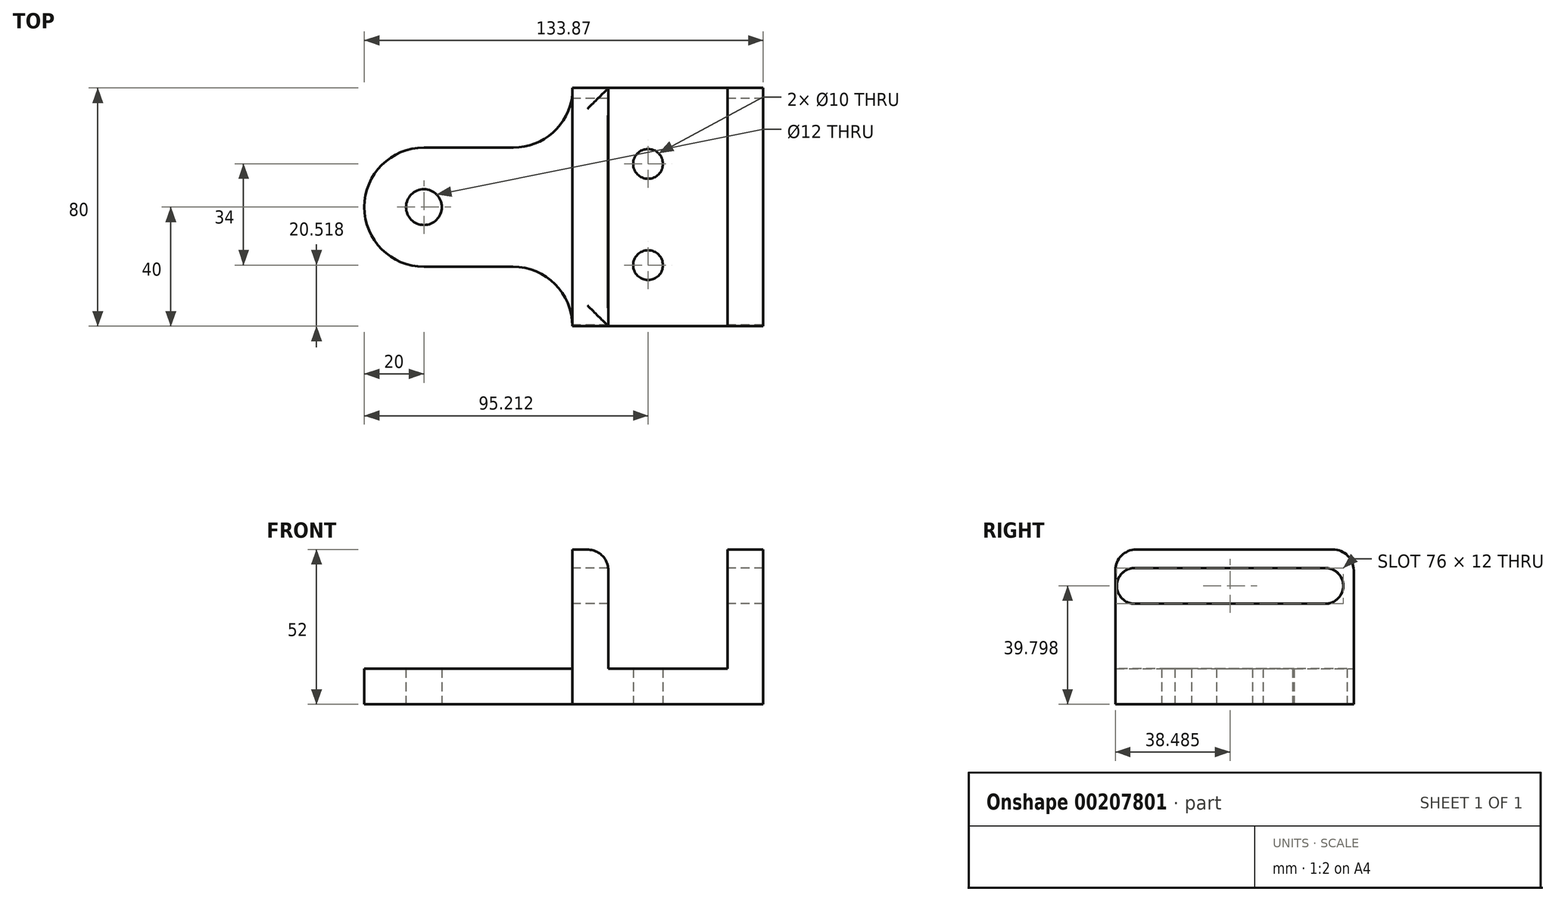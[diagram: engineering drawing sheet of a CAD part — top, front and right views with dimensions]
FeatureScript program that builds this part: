
annotation { "Feature Type Name" : "Feature", "Feature Type Description" : "" }
export const myFeature = defineFeature(function(context is Context, id is Id, definition is map)
    precondition{}
    {
        {
            var Q0;
            Q0=qCreatedBy(makeId("Top.planeOp"),FACE);
            var sketch = newSketch(context, id + "F0", { "sketchPlane" : qUnion([Q0])});
            skCircle(sketch, "E0", {"center": v(0, 0) * mm, "radius": 6 * mm});
            skArc(sketch, "E1", {"start": v(0, 20) * mm, "mid": v(-20, 0) * mm, "end": v(0, -20) * mm});
            skLineSegment(sketch, "E2", {"start": v(0, 20) * mm, "end": v(30, 20) * mm});
            skLineSegment(sketch, "E3", {"start": v(0, -20) * mm, "end": v(29.86, -20) * mm});
            skArc(sketch, "E4", {"start": v(29.97, 20) * mm, "mid": v(44.13, 25.85) * mm, "end": v(50, 40) * mm});
            skArc(sketch, "E5", {"start": v(29.83, -60) * mm, "mid": v(29.93, -60) * mm, "end": v(30.03, -60) * mm});
            skLineSegment(sketch, "E6.trimOffspring", {"start": v(30.03, -60) * mm, "end": v(30.03, -60) * mm});
            skLineSegment(sketch, "E7", {"start": v(49.86, -40) * mm, "end": v(102, -40) * mm});
            skArc(sketch, "E8.trimOffspring", {"start": v(49.86, -40) * mm, "mid": v(44, -25.86) * mm, "end": v(29.86, -20) * mm});
            skPoint(sketch, "E9.end.orphan", {"position": v(127.5, 40) * mm});
            skLineSegment(sketch, "E10", {"start": v(50, 40) * mm, "end": v(102, 40) * mm});
            skPoint(sketch, "E11.orphan", {"position": v(-57.63, 40) * mm});
            skLineSegment(sketch, "E12", {"start": v(113.87, 33) * mm, "end": v(113.87, -33) * mm});
            skLineSegment(sketch, "E13.top", {"start": v(114, 33) * mm, "end": v(102, 33) * mm});
            skLineSegment(sketch, "E13.right", {"start": v(102, 40) * mm, "end": v(102, 33) * mm});
            skLineSegment(sketch, "E14.MirrorCS", {"start": v(114, -33) * mm, "end": v(102, -33) * mm});
            skLineSegment(sketch, "E15.MirrorCS", {"start": v(102, -40) * mm, "end": v(102, -33) * mm});
            skCircle(sketch, "E16", {"center": v(75.21, 14.52) * mm, "radius": 5 * mm});
            skCircle(sketch, "E17", {"center": v(75.21, -19.48) * mm, "radius": 5 * mm});
            skSolve(sketch);
        }
        {
            var Q0;
            Q0=makeQuery(id+"F0.imprint","IMPRINT",FACE,{"disambiguationData":[TD([[makeQuery(id+"F0.imprint","IMPRINT",EDGE,{"derivedFrom":sQuery(id+"F0.wireOp",EDGE,"E0")}),-1.0]])]});
            extrude(context, id + "F1", {"entities" : qUnion([Q0]), "depth" : 12 * mm});
        }
        {
            var Q0;
            Q0=makeQuery(id+"F1.opExtrude","SWEPT_FACE",FACE,{"disambiguationData":[OSD([sQuery(id+"F0.wireOp",EDGE,"E10")])]});
            var sketch = newSketch(context, id + "F2", { "sketchPlane" : qUnion([Q0])});
            skLineSegment(sketch, "E18.bottom", {"start": v(-113.87, 0) * mm, "end": v(-101.87, 0) * mm});
            skLineSegment(sketch, "E18.top", {"start": v(-113.87, 52) * mm, "end": v(-101.87, 52) * mm});
            skLineSegment(sketch, "E18.left", {"start": v(-113.87, 0) * mm, "end": v(-113.87, 52) * mm});
            skLineSegment(sketch, "E18.right", {"start": v(-101.87, 0) * mm, "end": v(-101.87, 52) * mm});
            skLineSegment(sketch, "E19.bottom", {"start": v(-61.87, 0) * mm, "end": v(-49.87, 0) * mm});
            skLineSegment(sketch, "E19.top", {"start": v(-61.87, 52) * mm, "end": v(-49.87, 52) * mm});
            skLineSegment(sketch, "E19.left", {"start": v(-61.87, 0) * mm, "end": v(-61.87, 52) * mm});
            skLineSegment(sketch, "E19.right", {"start": v(-49.87, 0) * mm, "end": v(-49.87, 52) * mm});
            skSolve(sketch);
        }
        {
            var Q0;
            {var subQ1=sQuery(id+"F2.wireOp",EDGE,"E18.top");Q0=makeQuery(id+"F2.imprint","IMPRINT",FACE,{"disambiguationData":[TD([[makeQuery(id+"F2.imprint","IMPRINT",EDGE,{"derivedFrom":subQ1}),-1.0]])]});}
            var Q1;
            {var subQ2=sQuery(id+"F2.wireOp",EDGE,"E19.top");Q1=makeQuery(id+"F2.imprint","IMPRINT",FACE,{"disambiguationData":[TD([[makeQuery(id+"F2.imprint","IMPRINT",EDGE,{"derivedFrom":subQ2}),-1.0]])]});}
            var Q2;
            {var subQ1=sQuery(id+"F0.wireOp",EDGE,"E10");var subQ2=makeQuery(id+"F1.opExtrude","SWEPT_EDGE",EDGE,{"disambiguationData":[OSD([sQuery(id+"F0.wireOp",EDGE,"E4"),subQ1])]});Q2=makeQuery(id+"F2.imprint","IMPRINT",FACE,{"disambiguationData":[TD([[makeQuery(id+"F2.imprint","IMPRINT",EDGE,{"derivedFrom":subQ2}),-1.0]])]});}
            extrude(context, id + "F3", {"entities" : qUnion([Q0, Q1, Q2]), "operationType" : NewBodyOperationType.ADD, "oppositeDirection" : true, "depth" : 80 * mm});
        }
        {
            var Q0;
            Q0=makeQuery(id+"F3.opExtrude","CAP_EDGE",EDGE,{"disambiguationData":[OSD([sQuery(id+"F2.wireOp",EDGE,"E18.top")])],"isStart":true});
            var Q1;
            Q1=makeQuery(id+"F3.opExtrude","CAP_EDGE",EDGE,{"disambiguationData":[OSD([sQuery(id+"F2.wireOp",EDGE,"E19.top")])],"isStart":true});
            var Q2;
            Q2=makeQuery(id+"F3.opExtrude","CAP_EDGE",EDGE,{"disambiguationData":[OSD([sQuery(id+"F2.wireOp",EDGE,"E19.top")])],"isStart":false});
            var Q3;
            Q3=makeQuery(id+"F3.opExtrude","CAP_EDGE",EDGE,{"disambiguationData":[OSD([sQuery(id+"F2.wireOp",EDGE,"E18.top")])],"isStart":false});
            var Q4;
            Q4=makeQuery(id+"F3.opExtrude","SWEPT_EDGE",EDGE,{"disambiguationData":[OSD([sQuery(id+"F2.wireOp",EDGE,"E19.top"),sQuery(id+"F2.wireOp",EDGE,"E19.left")])]});
            fillet(context, id + "F4", {"entities" : qUnion([Q0, Q1, Q2, Q3, Q4]), "radius" : 7 * mm, "tangentPropagation" : true, "allowEdgeOverflow" : false});
        }
        {
            var Q0;
            Q0=makeQuery(id+"F3.opExtrude","SWEPT_FACE",FACE,{"disambiguationData":[OSD([sQuery(id+"F2.wireOp",EDGE,"E19.right")])]});
            var sketch = newSketch(context, id + "F5", { "sketchPlane" : qUnion([Q0])});
            skLineSegment(sketch, "E20.bottom", {"start": v(-30.48, 45.8) * mm, "end": v(33.52, 45.8) * mm});
            skLineSegment(sketch, "E20.top", {"start": v(-30.48, 33.8) * mm, "end": v(33.52, 33.8) * mm});
            skLineSegment(sketch, "E20.left", {"start": v(-30.48, 45.8) * mm, "end": v(-30.48, 33.8) * mm});
            skLineSegment(sketch, "E20.right", {"start": v(33.52, 45.8) * mm, "end": v(33.52, 33.8) * mm});
            skArc(sketch, "E21", {"start": v(-30.48, 45.8) * mm, "mid": v(-36.48, 39.8) * mm, "end": v(-30.48, 33.8) * mm});
            skArc(sketch, "E22", {"start": v(33.52, 33.8) * mm, "mid": v(39.52, 39.8) * mm, "end": v(33.52, 45.8) * mm});
            skSolve(sketch);
        }
        {
            var Q0;
            Q0=makeQuery(id+"F5.imprint","IMPRINT",FACE,{"disambiguationData":[TD([[makeQuery(id+"F5.imprint","IMPRINT",EDGE,{"derivedFrom":sQuery(id+"F5.wireOp",EDGE,"E20.bottom")}),-1.0]])]});
            var Q1;
            Q1=makeQuery(id+"F5.imprint","IMPRINT",FACE,{"disambiguationData":[TD([[makeQuery(id+"F5.imprint","IMPRINT",EDGE,{"derivedFrom":sQuery(id+"F5.wireOp",EDGE,"E20.left")}),-1.0]])]});
            var Q2;
            Q2=makeQuery(id+"F5.imprint","IMPRINT",FACE,{"disambiguationData":[TD([[makeQuery(id+"F5.imprint","IMPRINT",EDGE,{"derivedFrom":sQuery(id+"F5.wireOp",EDGE,"E20.right")}),1.0]])]});
            extrude(context, id + "F6", {"entities" : qUnion([Q0, Q1, Q2]), "operationType" : NewBodyOperationType.REMOVE, "oppositeDirection" : true, "depth" : 77.1 * mm});
        }
    });
